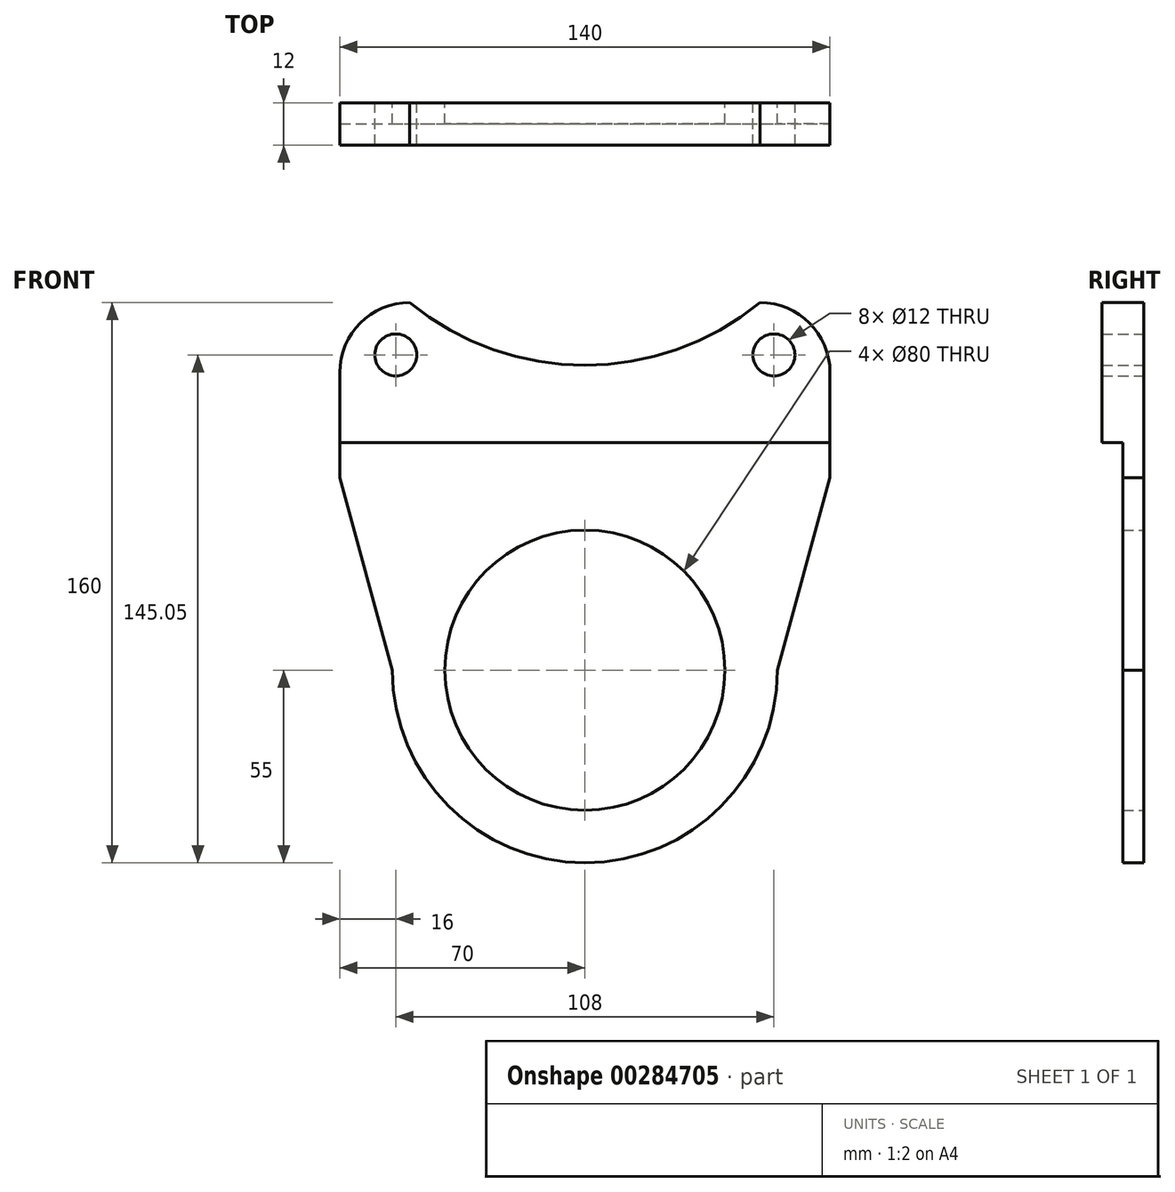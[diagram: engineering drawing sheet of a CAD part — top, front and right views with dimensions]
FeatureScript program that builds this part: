
annotation { "Feature Type Name" : "Feature", "Feature Type Description" : "" }
export const myFeature = defineFeature(function(context is Context, id is Id, definition is map)
    precondition{}
    {
        {
            var Q0;
            Q0=qCreatedBy(makeId("Front.planeOp"),FACE);
            var sketch = newSketch(context, id + "F0", { "sketchPlane" : qUnion([Q0])});
            skCircle(sketch, "E0", {"center": v(0, 0) * mm, "radius": 40 * mm});
            skCircle(sketch, "E1", {"center": v(0, 0) * mm, "radius": 55 * mm});
            skPoint(sketch, "E2", {"position": v(0, 55) * mm});
            skLineSegment(sketch, "E3", {"start": v(0, 55) * mm, "end": v(70, 55) * mm});
            skLineSegment(sketch, "E4", {"start": v(0, 55) * mm, "end": v(-70, 55) * mm});
            skLineSegment(sketch, "E5", {"start": v(-70, 55) * mm, "end": v(-70, 85) * mm});
            skLineSegment(sketch, "E6", {"start": v(-50, 105) * mm, "end": v(50, 105) * mm});
            skLineSegment(sketch, "E7", {"start": v(70, 85) * mm, "end": v(70, 55) * mm});
            skPoint(sketch, "E8", {"position": v(-54, 90.05) * mm});
            skCircle(sketch, "E9", {"center": v(-54, 90.05) * mm, "radius": 6 * mm});
            skLineSegment(sketch, "E10", {"start": v(-70, 55) * mm, "end": v(-55, 0) * mm});
            skLineSegment(sketch, "E11", {"start": v(70, 55) * mm, "end": v(55, 0) * mm});
            skCircle(sketch, "E12.MirrorC", {"center": v(54, 90.05) * mm, "radius": 6 * mm});
            skPoint(sketch, "E13.visualSharp", {"position": v(-70, 105) * mm});
            skArc(sketch, "E13.filletArc", {"start": v(-50, 105) * mm, "mid": v(-64.14, 99.14) * mm, "end": v(-70, 85) * mm});
            skPoint(sketch, "E14.visualSharp", {"position": v(70, 105) * mm});
            skArc(sketch, "E14.filletArc", {"start": v(70, 85) * mm, "mid": v(64.14, 99.14) * mm, "end": v(50, 105) * mm});
            skArc(sketch, "E15", {"start": v(-50, 105) * mm, "mid": v(0, 87.07) * mm, "end": v(50, 105) * mm});
            skSolve(sketch);
        }
        {
            var Q0;
            {var subQ0=sQuery(id+"F0.wireOp",EDGE,"E3");Q0=makeQuery(id+"F0.imprint","IMPRINT",FACE,{"disambiguationData":[TD([[makeQuery(id+"F0.imprint","IMPRINT",EDGE,{"derivedFrom":subQ0}),-1.0]])]});}
            var Q1;
            {var subQ0=sQuery(id+"F0.wireOp",EDGE,"E4");Q1=makeQuery(id+"F0.imprint","IMPRINT",FACE,{"disambiguationData":[TD([[makeQuery(id+"F0.imprint","IMPRINT",EDGE,{"derivedFrom":subQ0}),1.0]])]});}
            var Q2;
            Q2=makeQuery(id+"F0.imprint","IMPRINT",FACE,{"disambiguationData":[TD([[makeQuery(id+"F0.imprint","IMPRINT",EDGE,{"derivedFrom":sQuery(id+"F0.wireOp",EDGE,"E0")}),-1.0]])]});
            var Q3;
            Q3=makeQuery(id+"F0.imprint","IMPRINT",FACE,{"disambiguationData":[TD([[makeQuery(id+"F0.imprint","IMPRINT",EDGE,{"derivedFrom":sQuery(id+"F0.wireOp",EDGE,"E3")}),1.0]])]});
            extrude(context, id + "F1", {"entities" : qUnion([Q0, Q1, Q2, Q3]), "depth" : 12 * mm});
        }
        {
            var Q0;
            Q0=makeQuery(id+"F1.opExtrude","CAP_FACE",FACE,{"disambiguationData":[OSD([sQuery(id+"F0.wireOp",EDGE,"E0"),sQuery(id+"F0.wireOp",EDGE,"E1"),sQuery(id+"F0.wireOp",EDGE,"E5"),sQuery(id+"F0.wireOp",EDGE,"E7"),sQuery(id+"F0.wireOp",EDGE,"E9"),sQuery(id+"F0.wireOp",EDGE,"E10"),sQuery(id+"F0.wireOp",EDGE,"E11"),sQuery(id+"F0.wireOp",EDGE,"E12.MirrorC"),sQuery(id+"F0.wireOp",EDGE,"E13.filletArc"),sQuery(id+"F0.wireOp",EDGE,"E14.filletArc"),sQuery(id+"F0.wireOp",EDGE,"E15")])],"isStart":false});
            var sketch = newSketch(context, id + "F2", { "sketchPlane" : qUnion([Q0])});
            skCircle(sketch, "E16.0", {"center": v(0, 0) * mm, "radius": 40 * mm});
            skArc(sketch, "E17.1", {"start": v(-55, 0) * mm, "mid": v(0, -55) * mm, "end": v(55, 0) * mm});
            skLineSegment(sketch, "E18", {"start": v(0, -55) * mm, "end": v(0, 65) * mm, "construction": true});
            skPoint(sketch, "E18.endSnap0", {"position": v(0, -55) * mm});
            skLineSegment(sketch, "E19.0", {"start": v(70, 55) * mm, "end": v(55, 0) * mm});
            skLineSegment(sketch, "E20.1", {"start": v(70, 65) * mm, "end": v(70, 55) * mm});
            skLineSegment(sketch, "E21.1", {"start": v(70, 85) * mm, "end": v(70, 55) * mm});
            skLineSegment(sketch, "E21.2", {"start": v(-70, 55) * mm, "end": v(-55, 0) * mm});
            skLineSegment(sketch, "E22.3", {"start": v(-70, 55) * mm, "end": v(-70, 65) * mm});
            skLineSegment(sketch, "E23", {"start": v(0, 65) * mm, "end": v(70, 65) * mm});
            skLineSegment(sketch, "E24", {"start": v(0, 65) * mm, "end": v(-70, 65) * mm});
            skPoint(sketch, "E25.orphan", {"position": v(-70, 85) * mm});
            skSolve(sketch);
        }
        {
            var Q0;
            Q0=qSketchRegion(id+"F2",true);
            extrude(context, id + "F3", {"entities" : qUnion([Q0]), "operationType" : NewBodyOperationType.REMOVE, "oppositeDirection" : true, "depth" : 6 * mm});
        }
    });
